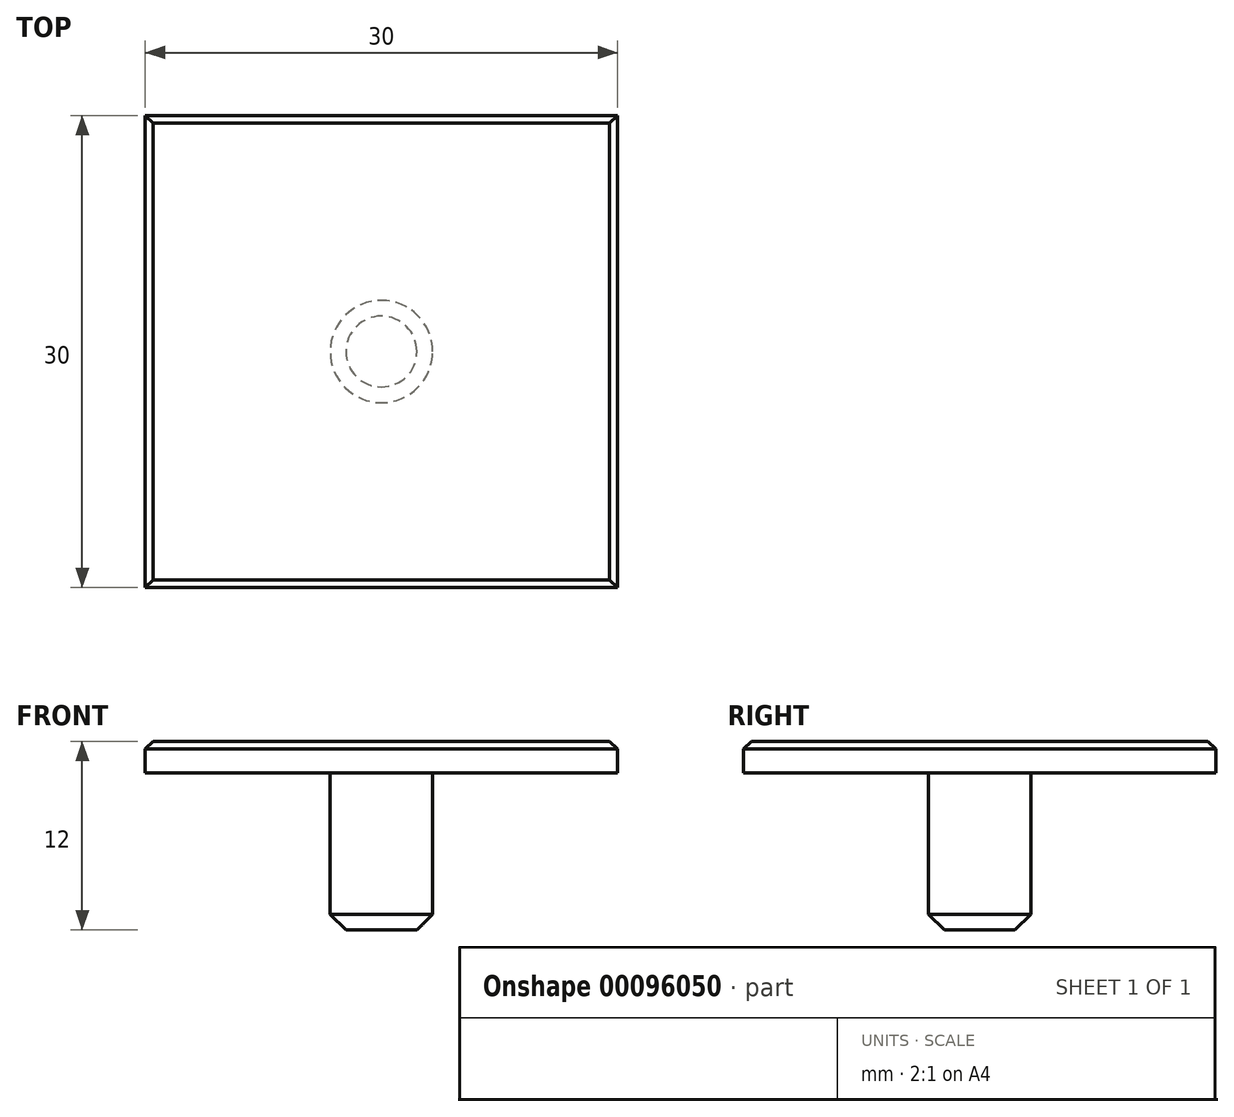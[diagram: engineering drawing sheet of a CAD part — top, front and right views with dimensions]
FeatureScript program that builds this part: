
annotation { "Feature Type Name" : "Feature", "Feature Type Description" : "" }
export const myFeature = defineFeature(function(context is Context, id is Id, definition is map)
    precondition{}
    {
        {
            var Q0;
            Q0=qCreatedBy(makeId("Top.planeOp"),FACE);
            var sketch = newSketch(context, id + "F0", { "sketchPlane" : qUnion([Q0])});
            skLineSegment(sketch, "E0.bottom", {"start": v(15, -15) * mm, "end": v(-15, -15) * mm});
            skLineSegment(sketch, "E0.top", {"start": v(15, 15) * mm, "end": v(-15, 15) * mm});
            skLineSegment(sketch, "E0.left", {"start": v(15, -15) * mm, "end": v(15, 15) * mm});
            skLineSegment(sketch, "E0.right", {"start": v(-15, -15) * mm, "end": v(-15, 15) * mm});
            skPoint(sketch, "E0.middle", {"position": v(0, 0) * mm});
            skSolve(sketch);
        }
        {
            var Q0;
            Q0 = qSketchRegion(id + "F0", true);
            extrude(context, id + "F1", {"entities" : qUnion([Q0]), "depth" : 2 * mm});
        }
        {
            var Q0;
            Q0=makeQuery(id+"F1.opExtrude","CAP_EDGE",EDGE,{"disambiguationData":[OSD([sQuery(id+"F0.wireOp",EDGE,"E0.right")])],"isStart":false});
            var Q1;
            Q1=makeQuery(id+"F1.opExtrude","CAP_EDGE",EDGE,{"disambiguationData":[OSD([sQuery(id+"F0.wireOp",EDGE,"E0.top")])],"isStart":false});
            var Q2;
            Q2=makeQuery(id+"F1.opExtrude","CAP_EDGE",EDGE,{"disambiguationData":[OSD([sQuery(id+"F0.wireOp",EDGE,"E0.left")])],"isStart":false});
            var Q3;
            Q3=makeQuery(id+"F1.opExtrude","CAP_EDGE",EDGE,{"disambiguationData":[OSD([sQuery(id+"F0.wireOp",EDGE,"E0.bottom")])],"isStart":false});
            chamfer(context, id + "F2", {"entities" : qUnion([Q0, Q1, Q2, Q3]), "width" : .5 * mm, "tangentPropagation" : true});
        }
        {
            var Q0;
            Q0=qCreatedBy(makeId("Top.planeOp"),FACE);
            var sketch = newSketch(context, id + "F3", { "sketchPlane" : qUnion([Q0])});
            skCircle(sketch, "E1", {"center": v(0, 0) * mm, "radius": 3.25 * mm});
            skSolve(sketch);
        }
        {
            var Q0;
            Q0 = qSketchRegion(id + "F3", true);
            extrude(context, id + "F4", {"entities" : qUnion([Q0]), "operationType" : NewBodyOperationType.ADD, "oppositeDirection" : true, "depth" : 10 * mm});
        }
        {
            var Q0;
            Q0=makeQuery(id+"F4.opExtrude","CAP_EDGE",EDGE,{"disambiguationData":[OSD([sQuery(id+"F3.wireOp",EDGE,"E1")])],"isStart":false});
            chamfer(context, id + "F5", {"entities" : qUnion([Q0]), "width" : 1 * mm, "tangentPropagation" : true});
        }
    });
